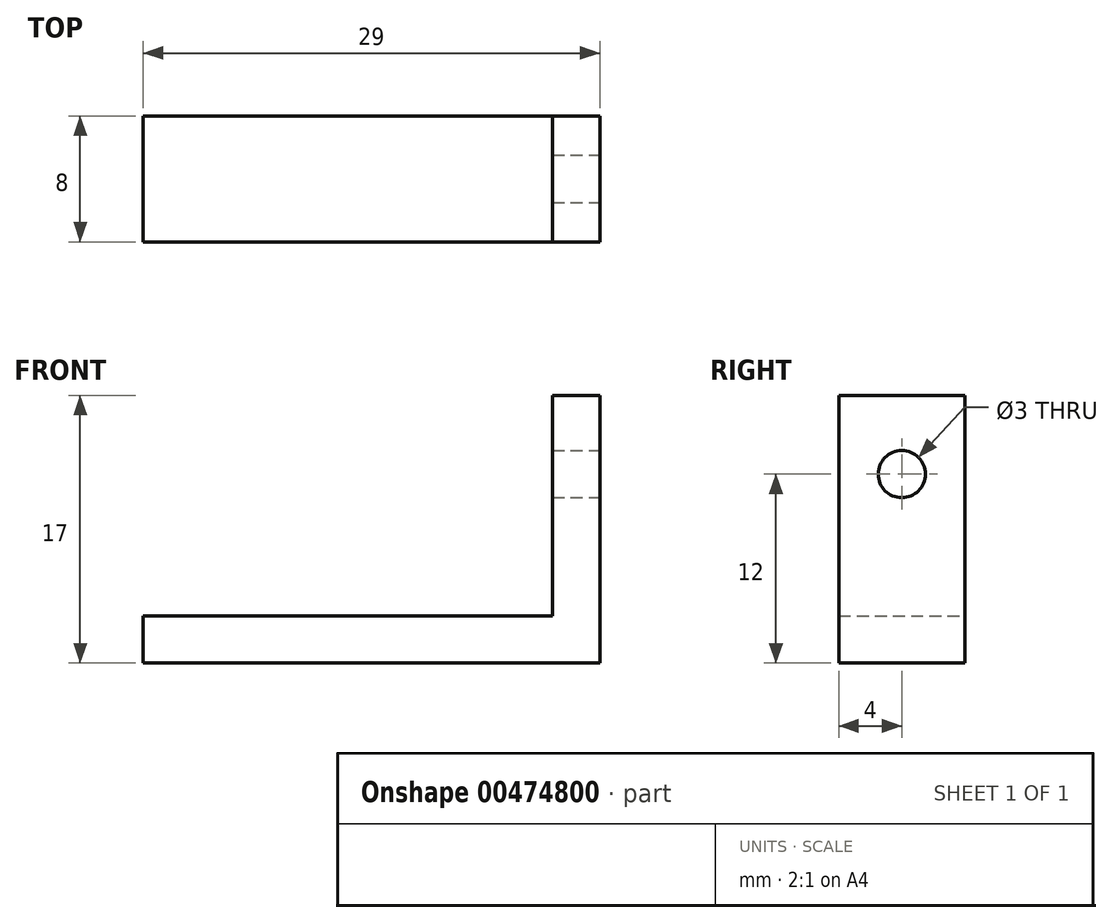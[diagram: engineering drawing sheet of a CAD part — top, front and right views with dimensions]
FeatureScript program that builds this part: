
annotation { "Feature Type Name" : "Feature", "Feature Type Description" : "" }
export const myFeature = defineFeature(function(context is Context, id is Id, definition is map)
    precondition{}
    {
        {
            var Q0;
            Q0=qCreatedBy(makeId("Front.planeOp"),FACE);
            var sketch = newSketch(context, id + "F0", { "sketchPlane" : qUnion([Q0])});
            skLineSegment(sketch, "E0.bottom", {"start": v(-1.5, 8.5) * mm, "end": v(1.5, 8.5) * mm});
            skLineSegment(sketch, "E0.top", {"start": v(-1.5, -8.5) * mm, "end": v(1.5, -8.5) * mm});
            skLineSegment(sketch, "E0.left", {"start": v(-1.5, 8.5) * mm, "end": v(-1.5, -5.5) * mm});
            skLineSegment(sketch, "E0.right", {"start": v(1.5, 8.5) * mm, "end": v(1.5, -8.5) * mm});
            skPoint(sketch, "E0.middle", {"position": v(0, 0) * mm});
            skLineSegment(sketch, "E1", {"start": v(-27.5, -5.5) * mm, "end": v(-1.5, -5.5) * mm});
            skLineSegment(sketch, "E2", {"start": v(-27.5, -8.5) * mm, "end": v(-1.5, -8.5) * mm});
            skLineSegment(sketch, "E3", {"start": v(-27.5, -5.5) * mm, "end": v(-27.5, -8.5) * mm});
            skSolve(sketch);
        }
        {
            var Q0;
            Q0 = qSketchRegion(id + "F0", true);
            extrude(context, id + "F1", {"entities" : qUnion([Q0]), "depth" : 8 * mm});
        }
        {
            var Q0;
            Q0=makeQuery(id+"F1.opExtrude","SWEPT_FACE",FACE,{"disambiguationData":[OSD([sQuery(id+"F0.wireOp",EDGE,"E0.right")])]});
            var sketch = newSketch(context, id + "F2", { "sketchPlane" : qUnion([Q0])});
            skCircle(sketch, "E4", {"center": v(-4, 3.5) * mm, "radius": 1.5 * mm});
            skPoint(sketch, "E4.centerSnap0", {"position": v(-4, 8.5) * mm});
            skSolve(sketch);
        }
        {
            var Q0;
            Q0=makeQuery(id+"F2.imprint","IMPRINT",FACE,{"disambiguationData":[TD([[makeQuery(id+"F2.imprint","IMPRINT",EDGE,{"derivedFrom":sQuery(id+"F2.wireOp",EDGE,"E4")}),1.0]])]});
            extrude(context, id + "F3", {"entities" : qUnion([Q0]), "operationType" : NewBodyOperationType.REMOVE, "oppositeDirection" : true, "depth" : 25 * mm});
        }
    });
